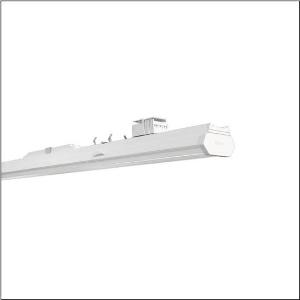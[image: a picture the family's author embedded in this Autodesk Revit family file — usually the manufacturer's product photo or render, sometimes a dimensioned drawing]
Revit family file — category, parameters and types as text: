
# Revit family: licross_r__11_protected_mo_51td1bdn49xg3c_d1bb
name_source: partatom
category: Lighting Fixtures
units: mm (PartAtom-declared; Revit-internal decimal feet)

## family parameters
Cut with Voids When Loaded = No
Host = Face
Light Source = No
Part Type = Normal
Room Calculation Point = No
Round Connector Dimension = Use Diameter
Shared = No

## types (1)
- --- (1 x LED, 920 lm, 6.8 W, 4000K)
    Apparent Load = 7 VA
    CIE Flux Codes = 54 82 95 97 100
    Color Rendering = 80
    Color Temperature = 4000K
    Default Elevation = 1800 mm
    Description = Licross® 11 Protected MO, luminaire insert, of sheet steel, galvanised, coil coated, white, length: 1.500mm, width: 90mm, height: 101mm, LED rated luminous flux: 9.370lm, light colour: 840, control gear: DALI 2 (for two DALI lines), with plug, 6-pole, with phase selection, for trunking rail, 14-core, mains connection: 220..240V, AC, 50/60Hz, rated input power: 61W, for trunking rail, 14-core, halogen-free wiring, for emergency light function, converter,control gear: single battery element, battery: LiFePO4, 9Ah, primary optical cover: cover, of PMMA, light emission: direct distribution, primary light characteristic: symmetric, protection rating (complete): IP54, insulation class (complete): insulation class I (protective earthing), certification: CE, UKCA, protection symbol: D if used in an environment with non-conductive dust loads with corresponding accessories, impact resistance: IK06, permissible ambient temperature for indoor applications: +5..+35°C, standard: EN 60598-2-22, LABS conformity tested according to VDMA 24364:2018-05, reducing of maximum allowable ambient temperature of 5°C with ceiling mounting, corresponds to IFS (International Featured Standards) requirements for safety and quality in the food industry, packaging unit: 1 piece
    Height = 92 mm
    Lamp = 1 x LED
    Lamp Light Flux = 920 lm
    Lamp Power = 6.8 W
    Lamp count = 1
    Length = 1500 mm
    Luminous efficacy = 135 lm/W
    Manufacturer = Siteco
    ModVariant = No
    Model = 51TD1BDN49XG3C
    Mounting Place = Ceiling
    Mounting Type = Pendant
    Number of Poles = 1
    OnlyDefault = Yes
    Power Factor = 1
    Product Name = Licross® 11 Protected MO
    Product group = luminaire insert
    ProductGroupID = 901
    Protection Class = Protection class I
    Protection Degree = IP 54
    RLX_Detail_Level = 1
    RLX_Emergency_Light_Flux = 0 lm
    RLX_Emergency_Type = 0
    RLX_Emergency_Type_DB = No
    RlxData = <blob elided: 24697 chars, md5=c435af1c>
    Socket = socket
    Standby Power = 0 W
    System Light Flux = 920 lm
    System Power = 7 W
    Type Comments = : emergency light operation: 3 h
    Type Image = l_1256145.jpg
    URL = http://relux.com
    VarID = @adj_059927
    Voltage = 0 V
    Weight = 0.00 kg
    Width = 88 mm

## geometry (parser evidence)
native form markers: Blend x4, Sweep x10
no freeform markers — native parametric forms only
